# Revit family: Electrical_Equipment-Poke_Through-Hubbell_Wiring-System_One-S1R8_JNC3
name_source: partatom
category: Electrical Fixtures
revit_build: Autodesk Revit 2015 (Build: 20140606_1530(x64)
units: mm (PartAtom-declared; Revit-internal decimal feet)

## types (1)
- S1R8JNC3 Junction Box
    Amperage Max Limit Note = Max (5) 20 Amp Duplex Circuit
    Assembly Code = D5020115
    Center Bottom Power = 2400 VA
    Center Bottom Subplate = Center Subplate : S1R8CSPK
    Center Middle Power = 2400 VA
    Center Middle Subplate = Center Subplate : S1R8CSPK
    Center Top Power = 2400 VA
    Center Top Subplate = Center Subplate : S1R8CSPK
    Conduit Connector 1 Description = Conduit Connector 1
    Conduit Connector 2 Description = Conduit Connector 1
    Conduit Connector 3 Description = Conduit Connector 1
    Conduit Connector 4 Description = Conduit Connector 1
    Cover Material = Metal-Hubbell-Aluminum
    Default Elevation = 0' - 0"
    Description = System One - 8" Poke Through
    Electrical Connector Description = Power Connector
    Hardware Material = Metal-Hubbell-Steel
    Left Side Power = 2400 VA
    Left Side Subplate = Left Subplate : S1R8PSPZ
    Load Classification = Power
    Manufacturer = Hubbell-Wiring
    Model = S1R8PT
    Number of Poles = 1
    Power Factor = 1
    Product Documentation Link = http://ecatalog.hubbell-wiring.com
    Product Page URL = http://ecatalog.hubbell-wiring.com
    Product data url = https://bimobject.com
    Right Side Power = 2400 VA
    Right Side Subplate = Right Subplate : S1R8PSPZ
    URL = http://www.hubbell-wiring.com
    Voltage = 120 V

## geometry (parser evidence)
native form markers: Blend x28, Sweep x23
no freeform markers — native parametric forms only
